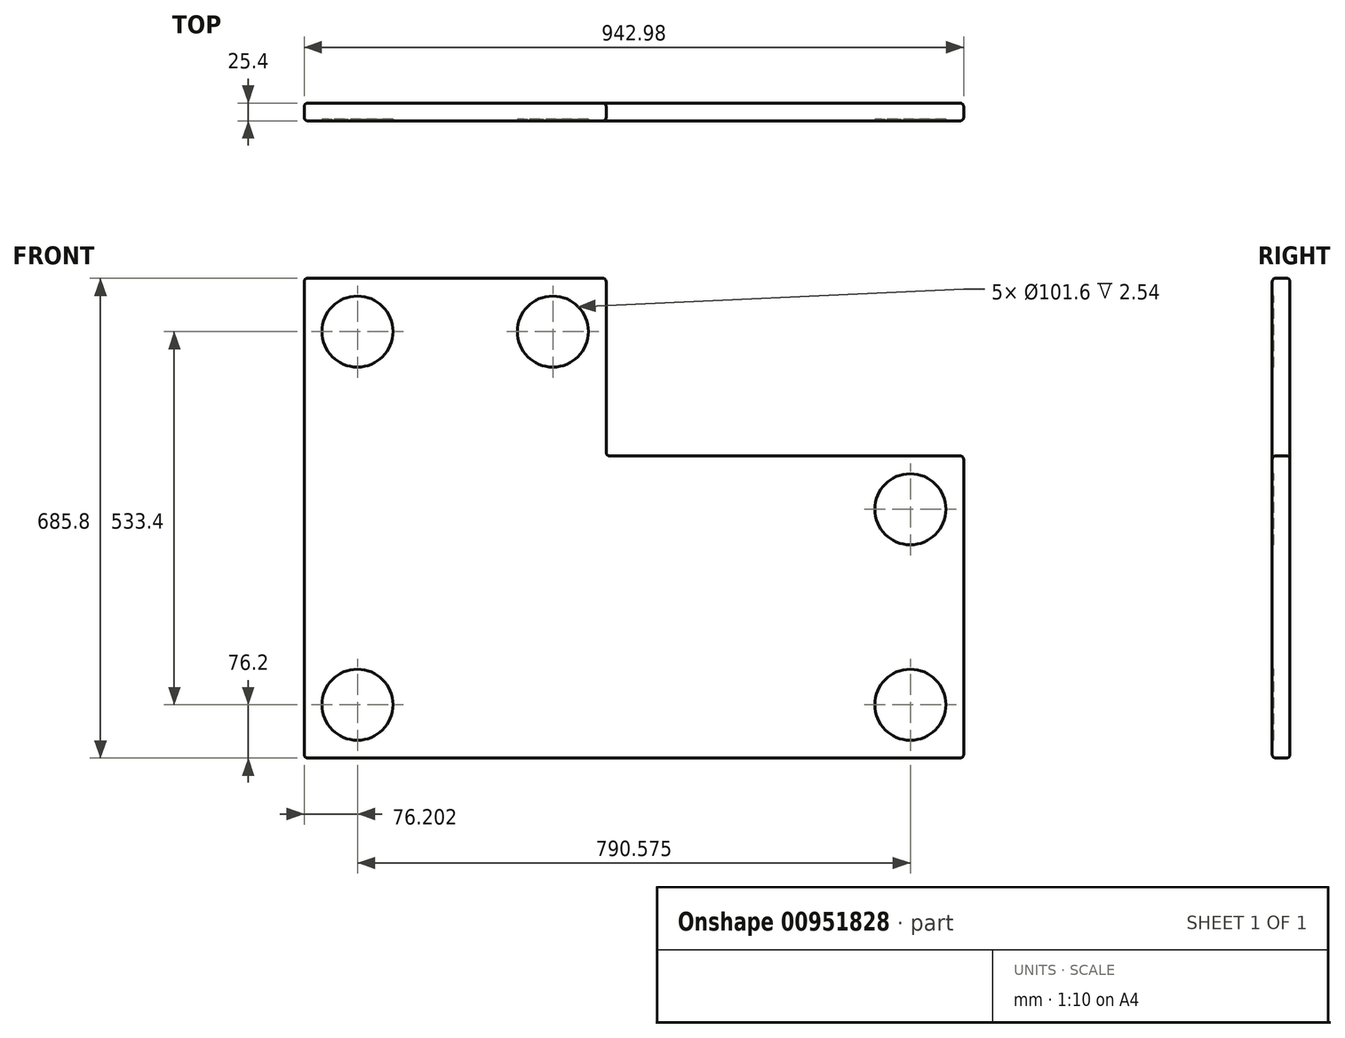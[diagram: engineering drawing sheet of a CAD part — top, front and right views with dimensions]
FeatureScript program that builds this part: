
annotation { "Feature Type Name" : "Feature", "Feature Type Description" : "" }
export const myFeature = defineFeature(function(context is Context, id is Id, definition is map)
    precondition{}
    {
        {
            var Q0;
            Q0=qCreatedBy(makeId("Front.planeOp"),FACE);
            var sketch = newSketch(context, id + "F0", { "sketchPlane" : qUnion([Q0])});
            skLineSegment(sketch, "E0.bottom", {"start": v(471.49, 342.9) * mm, "end": v(-471.49, 342.9) * mm, "construction": true});
            skLineSegment(sketch, "E0.top", {"start": v(471.49, -342.9) * mm, "end": v(-471.49, -342.9) * mm});
            skLineSegment(sketch, "E0.left", {"start": v(471.49, 342.9) * mm, "end": v(471.49, -342.9) * mm, "construction": true});
            skLineSegment(sketch, "E0.right", {"start": v(-471.49, 342.9) * mm, "end": v(-471.49, -342.9) * mm});
            skPoint(sketch, "E0.middle", {"position": v(0, 0) * mm});
            skLineSegment(sketch, "E1", {"start": v(-39.69, 342.9) * mm, "end": v(-39.69, 88.9) * mm});
            skLineSegment(sketch, "E2", {"start": v(-39.69, 88.9) * mm, "end": v(471.49, 88.9) * mm});
            skLineSegment(sketch, "E3", {"start": v(471.49, 88.9) * mm, "end": v(471.49, -342.9) * mm});
            skLineSegment(sketch, "E4", {"start": v(-471.49, 342.9) * mm, "end": v(-39.69, 342.9) * mm});
            skSolve(sketch);
        }
        {
            var Q0;
            Q0=makeQuery(id+"F0.imprint","IMPRINT",FACE,{"disambiguationData":[TD([[makeQuery(id+"F0.imprint","IMPRINT",EDGE,{"derivedFrom":sQuery(id+"F0.wireOp",EDGE,"E0.top")}),-1.0]])]});
            extrude(context, id + "F1", {"entities" : qUnion([Q0]), "depth" : 25.4 * mm, "offsetDistance" : 25 * mm});
        }
        {
            var Q0;
            Q0=makeQuery(id+"F1.opExtrude","CAP_FACE",FACE,{"disambiguationData":[OSD([sQuery(id+"F0.wireOp",EDGE,"E0.top"),sQuery(id+"F0.wireOp",EDGE,"E0.right"),sQuery(id+"F0.wireOp",EDGE,"E1"),sQuery(id+"F0.wireOp",EDGE,"E2"),sQuery(id+"F0.wireOp",EDGE,"E3"),sQuery(id+"F0.wireOp",EDGE,"E4")])],"isStart":false});
            var sketch = newSketch(context, id + "F2", { "sketchPlane" : qUnion([Q0])});
            skLineSegment(sketch, "E5", {"start": v(814.08, 0) * mm, "end": v(814.08, -344.07) * mm});
            skLineSegment(sketch, "E6", {"start": v(814.08, -344.07) * mm, "end": v(471.49, -342.9) * mm});
            skLineSegment(sketch, "E7", {"start": v(471.49, -342.9) * mm, "end": v(471.49, 0) * mm});
            skLineSegment(sketch, "E8", {"start": v(471.49, 0) * mm, "end": v(814.08, 0) * mm});
            skLineSegment(sketch, "E9", {"start": v(471.49, -342.9) * mm, "end": v(-471.49, 0) * mm});
            skLineSegment(sketch, "E10", {"start": v(-471.49, 0) * mm, "end": v(334.66, -261.25) * mm});
            skSolve(sketch);
        }
        {
            var Q0;
            {var subQ2=sQuery(id+"F2.wireOp",EDGE,"E7");Q0=makeQuery(id+"F2.imprint","IMPRINT",FACE,{"disambiguationData":[TD([[makeQuery(id+"F2.imprint","IMPRINT",EDGE,{"derivedFrom":subQ2}),-1.0]])]});}
            var sketch = newSketch(context, id + "F3", { "sketchPlane" : qUnion([Q0])});
            skCircle(sketch, "E11", {"center": v(-395.29, 266.7) * mm, "radius": 50.8 * mm});
            skCircle(sketch, "E12", {"center": v(-115.89, 266.7) * mm, "radius": 50.8 * mm});
            skCircle(sketch, "E13", {"center": v(-395.29, -266.7) * mm, "radius": 50.8 * mm});
            skCircle(sketch, "E14", {"center": v(395.29, -266.7) * mm, "radius": 50.8 * mm});
            skCircle(sketch, "E15", {"center": v(395.29, 12.7) * mm, "radius": 50.8 * mm});
            skSolve(sketch);
        }
        {
            var Q0;
            Q0 = qSketchRegion(id + "F3", true);
            extrude(context, id + "F4", {"entities" : qUnion([Q0]), "operationType" : NewBodyOperationType.REMOVE, "oppositeDirection" : true, "depth" : 2.54 * mm, "offsetDistance" : 25.4 * mm});
        }
        {
            var Q0;
            Q0=makeQuery(id+"F1.opExtrude","SWEPT_FACE",FACE,{"disambiguationData":[OSD([sQuery(id+"F0.wireOp",EDGE,"E0.top")])]});
            var Q1;
            Q1=makeQuery(id+"F1.opExtrude","SWEPT_FACE",FACE,{"disambiguationData":[OSD([sQuery(id+"F0.wireOp",EDGE,"E0.right")])]});
            var Q2;
            Q2=makeQuery(id+"F1.opExtrude","SWEPT_FACE",FACE,{"disambiguationData":[OSD([sQuery(id+"F0.wireOp",EDGE,"E3")])]});
            var Q3;
            Q3=makeQuery(id+"F1.opExtrude","SWEPT_FACE",FACE,{"disambiguationData":[OSD([sQuery(id+"F0.wireOp",EDGE,"E2")])]});
            var Q4;
            Q4=makeQuery(id+"F1.opExtrude","SWEPT_FACE",FACE,{"disambiguationData":[OSD([sQuery(id+"F0.wireOp",EDGE,"E1")])]});
            var Q5;
            Q5=makeQuery(id+"F1.opExtrude","SWEPT_FACE",FACE,{"disambiguationData":[OSD([sQuery(id+"F0.wireOp",EDGE,"E4")])]});
            fillet(context, id + "F5", {"entities" : qUnion([Q0, Q1, Q2, Q3, Q4, Q5]), "radius" : 5.08 * mm, "tangentPropagation" : true, "allowEdgeOverflow" : false});
        }
    });
